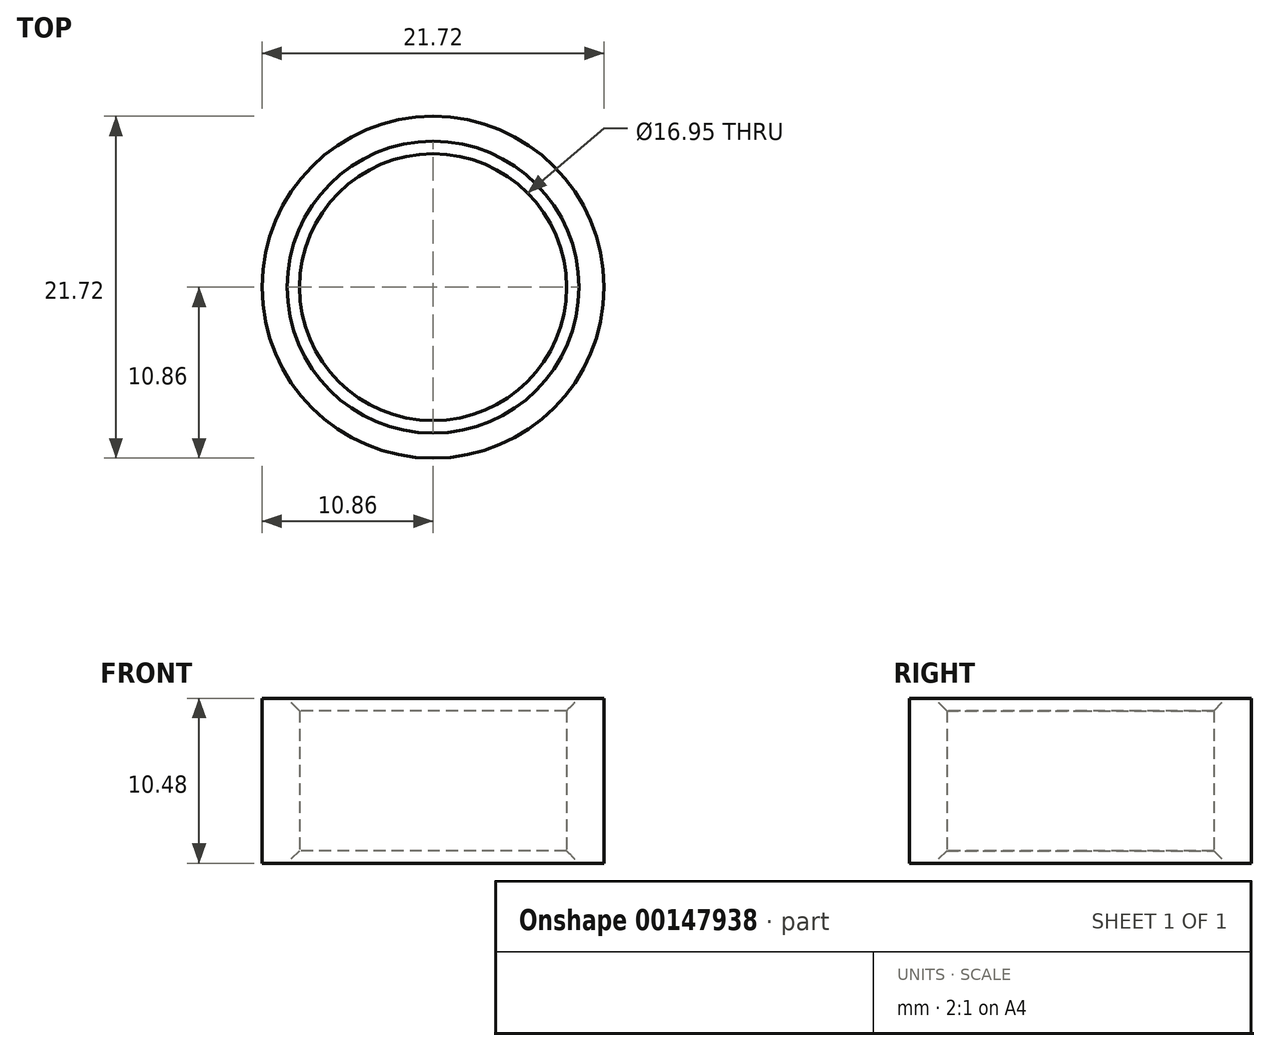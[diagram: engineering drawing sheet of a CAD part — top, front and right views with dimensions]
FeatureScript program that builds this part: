
annotation { "Feature Type Name" : "Feature", "Feature Type Description" : "" }
export const myFeature = defineFeature(function(context is Context, id is Id, definition is map)
    precondition{}
    {
        {
            var Q0;
            Q0=qCreatedBy(makeId("Top.planeOp"),FACE);
            var sketch = newSketch(context, id + "F0", { "sketchPlane" : qUnion([Q0])});
            skCircle(sketch, "E0", {"center": v(0, 0) * mm, "radius": 10.86 * mm});
            skCircle(sketch, "E1", {"center": v(0, 0) * mm, "radius": 8.48 * mm});
            skSolve(sketch);
        }
        {
            var Q0;
            Q0=qSketchRegion(id+"F0",true);
            extrude(context, id + "F1", {"entities" : qUnion([Q0]), "depth" : 10.48 * mm});
        }
        {
            var Q0;
            Q0=makeQuery(id+"F1.opExtrude","CAP_EDGE",EDGE,{"disambiguationData":[OSD([sQuery(id+"F0.wireOp",EDGE,"E1")])],"isStart":false});
            var Q1;
            Q1=makeQuery(id+"F1.opExtrude","CAP_EDGE",EDGE,{"disambiguationData":[OSD([sQuery(id+"F0.wireOp",EDGE,"E1")])],"isStart":true});
            chamfer(context, id + "F2", {"entities" : qUnion([Q0, Q1]), "width" : 0.8 * mm, "tangentPropagation" : true});
        }
    });
